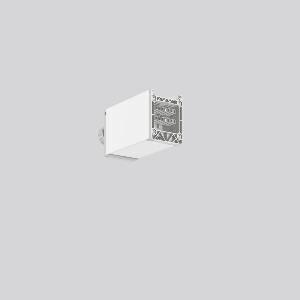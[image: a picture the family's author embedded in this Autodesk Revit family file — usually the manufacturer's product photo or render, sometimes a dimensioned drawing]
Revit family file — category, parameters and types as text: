
# Revit family: linedo_anfangseinspeisung_982859_002_f26b
name_source: partatom
category: Lighting Fixtures
units: mm (PartAtom-declared; Revit-internal decimal feet)

## family parameters
Cut with Voids When Loaded = No
Host = Face
Light Source = No
Part Type = Normal
Room Calculation Point = No
Round Connector Dimension = Use Diameter
Shared = No

## types (1)
- LINEDO Anfangseinspeisung
    Apparent Load = 0 VA
    Default Elevation = 1800 mm
    Description = Series: LINEDO
Initial power feed (short Version), 7-pole, connection socket. Housing: extruded aluminium profile, powder-coated. Cover made of plastic, surface like housing. LINEDO plug system, plastic, light grey. 1 cable gland (M25). Cable gland on side or on top. Convenient connection with flat connector.
Colour: white
Length: 134 mm
Width: 58 mm
Height: 76 mm
Weight: 278 g
    Height = 76 mm
    Lamp = 0 x
    Length = 134 mm
    Luminous efficacy = 0 lm/W
    Manufacturer = RZB
    ModVariant = No
    Model = 982859.002
    Mounting Place = Ceiling
    Mounting Type = Surface mounted
    Number of Poles = 1
    OnlyDefault = Yes
    Power Factor = 1
    Product Name = LINEDO Anfangseinspeisung
    Product group = Surface mounted continuous line luminaire system
    ProductGroupID = 310
    Protection Class = Protection class I
    Protection Degree = Degree of protection
    RLX_Detail_Level = 1
    RLX_Emergency_Light_Flux = 0 lm
    RLX_Emergency_Type = 0
    RLX_Emergency_Type_DB = No
    RlxData = <blob elided: 12853 chars, md5=c0fc0934>
    Standby Power = 0 W
    System Light Flux = 0 lm
    System Power = 0 W
    Type Comments = Product without accessories
    Type Image = 982859.002.jpg
    URL = http://relux.com
    VarID = ---
    Voltage = 0 V
    Weight = 0.00 kg
    Width = 58 mm

## geometry (parser evidence)
native form markers: Sweep x7
no freeform markers — native parametric forms only
